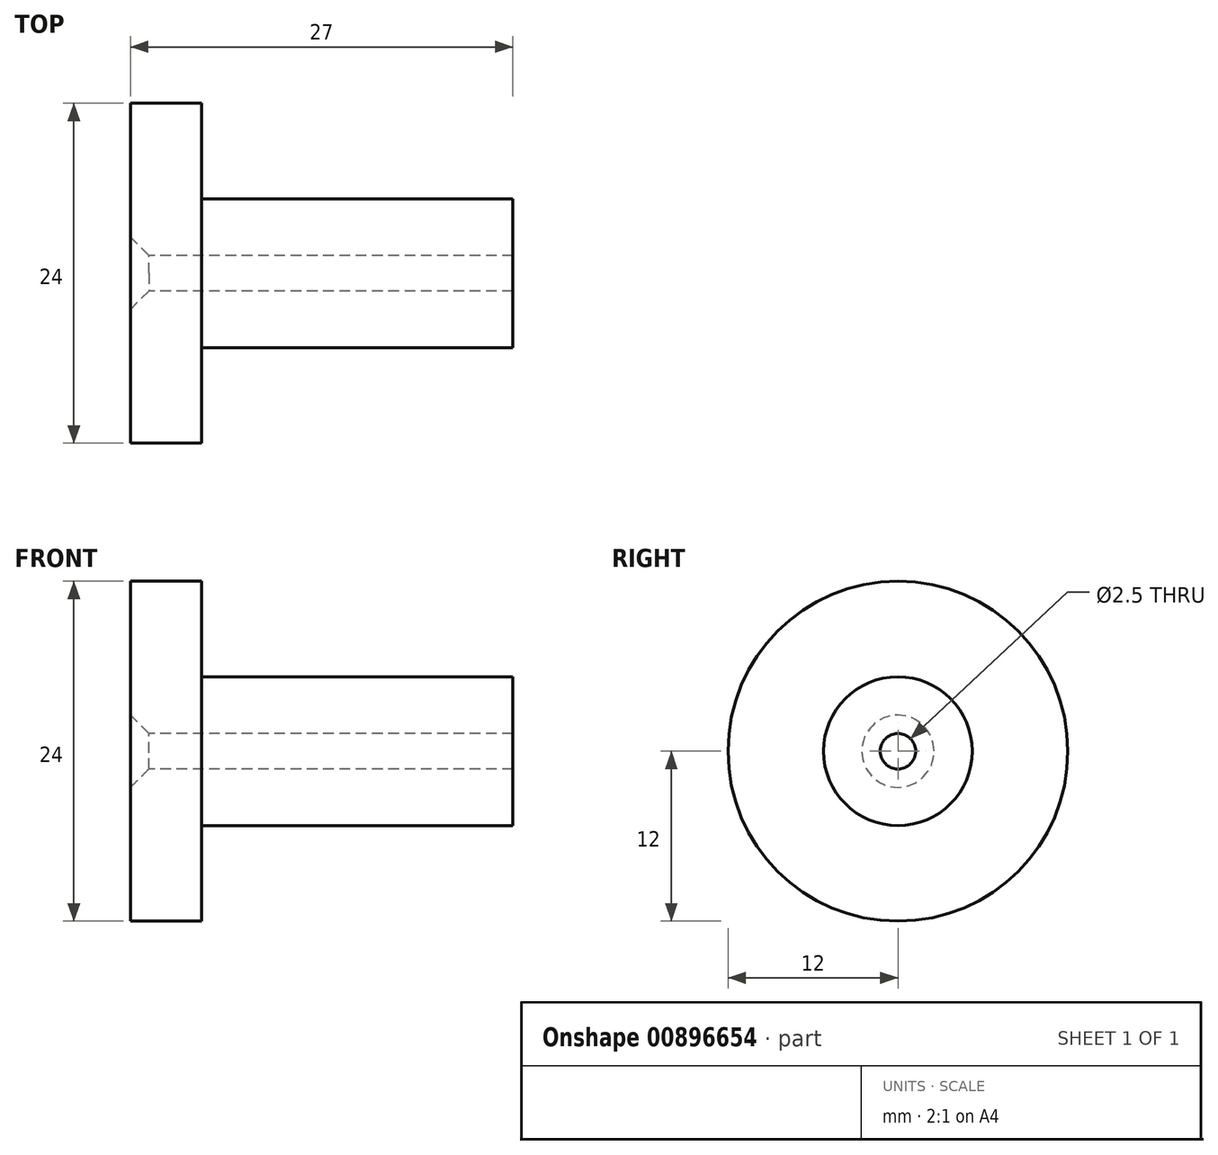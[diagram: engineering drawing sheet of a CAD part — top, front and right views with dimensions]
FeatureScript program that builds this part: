
annotation { "Feature Type Name" : "Feature", "Feature Type Description" : "" }
export const myFeature = defineFeature(function(context is Context, id is Id, definition is map)
    precondition{}
    {
        {
            var Q0;
            Q0=qCreatedBy(makeId("Front.planeOp"),FACE);
            var sketch = newSketch(context, id + "F0", { "sketchPlane" : qUnion([Q0])});
            skLineSegment(sketch, "E0", {"start": v(-17.7, 1.25) * mm, "end": v(9.3, 1.25) * mm});
            skLineSegment(sketch, "E1", {"start": v(9.3, 1.25) * mm, "end": v(9.3, 5.25) * mm});
            skLineSegment(sketch, "E2", {"start": v(9.3, 5.25) * mm, "end": v(-12.7, 5.25) * mm});
            skLineSegment(sketch, "E3", {"start": v(-12.7, 5.25) * mm, "end": v(-12.7, 12) * mm});
            skLineSegment(sketch, "E4", {"start": v(-12.7, 12) * mm, "end": v(-17.7, 12) * mm});
            skLineSegment(sketch, "E5", {"start": v(-17.7, 12) * mm, "end": v(-17.7, 1.25) * mm});
            skLineSegment(sketch, "E6", {"start": v(-32.13, 0) * mm, "end": v(26.64, 0) * mm, "construction": true});
            skSolve(sketch);
        }
        {
            var Q0;
            Q0 = qSketchRegion(id + "F0", true);
            var Q1;
            Q1=sQuery(id+"F0.wireOp",EDGE,"E6");
            revolve(context, id + "F1", {"surfaceOperationType" : NewSurfaceOperationType.NEW, "entities" : qUnion([Q0]), "axis" : qUnion([Q1]), "revolveType" : RevolveType.FULL});
        }
        {
            var Q0;
            Q0=makeQuery(id+"F1.opRevolve","SWEPT_EDGE",EDGE,{"disambiguationData":[OSD([sQuery(id+"F0.wireOp",EDGE,"E0"),sQuery(id+"F0.wireOp",EDGE,"E5")])]});
            chamfer(context, id + "F2", {"entities" : qUnion([Q0]), "width" : 1.3 * mm, "tangentPropagation" : true});
        }
    });
